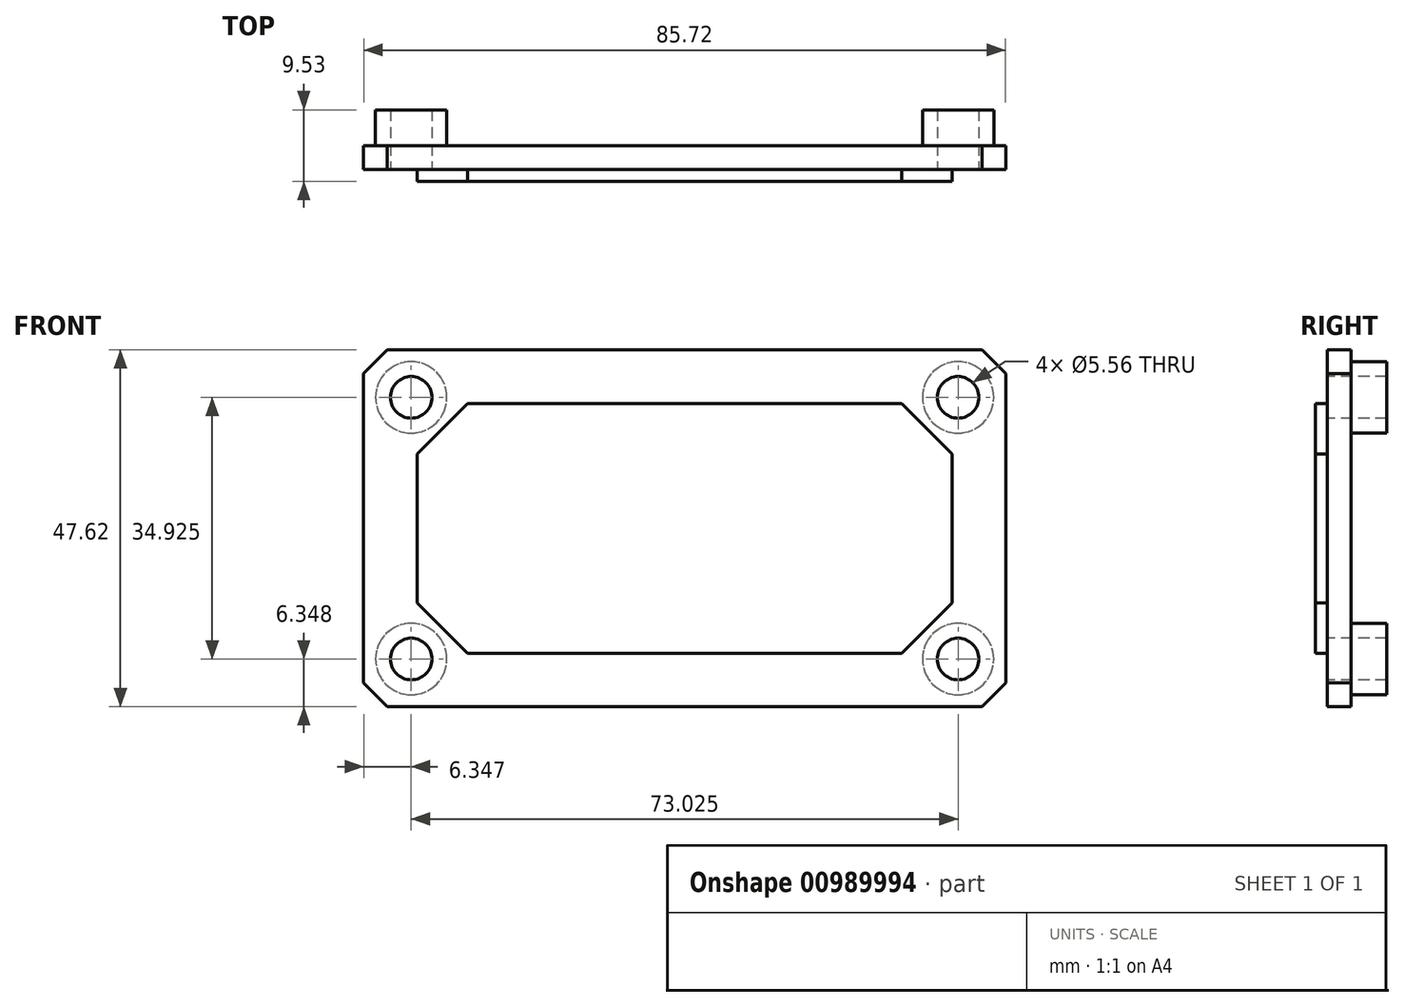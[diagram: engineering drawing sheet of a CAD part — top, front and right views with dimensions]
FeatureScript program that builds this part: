
annotation { "Feature Type Name" : "Feature", "Feature Type Description" : "" }
export const myFeature = defineFeature(function(context is Context, id is Id, definition is map)
    precondition{}
    {
        {
            var Q0;
            Q0=qCreatedBy(makeId("Front.planeOp"),FACE);
            var sketch = newSketch(context, id + "F0", { "sketchPlane" : qUnion([Q0])});
            skLineSegment(sketch, "E0.bottom", {"start": v(-42.86, 23.81) * mm, "end": v(42.86, 23.81) * mm});
            skLineSegment(sketch, "E0.top", {"start": v(-42.86, -23.81) * mm, "end": v(42.86, -23.81) * mm});
            skLineSegment(sketch, "E0.left", {"start": v(-42.86, 23.81) * mm, "end": v(-42.86, -23.81) * mm});
            skLineSegment(sketch, "E0.right", {"start": v(42.86, 23.81) * mm, "end": v(42.86, -23.81) * mm});
            skPoint(sketch, "E0.middle", {"position": v(0, 0) * mm});
            skLineSegment(sketch, "E1", {"start": v(-19.05, 0) * mm, "end": v(19.05, 0) * mm});
            skCircle(sketch, "E2", {"center": v(19.05, 0) * mm, "radius": 17.46 * mm});
            skCircle(sketch, "E3", {"center": v(-19.05, 0) * mm, "radius": 17.46 * mm});
            skCircle(sketch, "E4", {"center": v(-19.05, 0) * mm, "radius": 23.81 * mm, "construction": true});
            skLineSegment(sketch, "E5.0", {"start": v(-36.51, 17.46) * mm, "end": v(36.51, 17.46) * mm});
            skLineSegment(sketch, "E5.1", {"start": v(-36.51, 17.46) * mm, "end": v(-36.51, -17.46) * mm});
            skLineSegment(sketch, "E5.2", {"start": v(-36.51, -17.46) * mm, "end": v(36.51, -17.46) * mm});
            skLineSegment(sketch, "E5.3", {"start": v(36.51, 17.46) * mm, "end": v(36.51, -17.46) * mm});
            skCircle(sketch, "E6", {"center": v(-36.51, 17.46) * mm, "radius": 6.35 * mm, "construction": true});
            skCircle(sketch, "E7", {"center": v(-36.51, 17.46) * mm, "radius": 2.25 * mm});
            skCircle(sketch, "E8", {"center": v(-36.51, 17.46) * mm, "radius": 3.97 * mm});
            skLineSegment(sketch, "E9", {"start": v(-39.69, 23.81) * mm, "end": v(-42.86, 20.64) * mm});
            skCircle(sketch, "E10", {"center": v(-19.05, 0) * mm, "radius": 15.08 * mm});
            skCircle(sketch, "E11", {"center": v(19.05, 0) * mm, "radius": 15.08 * mm});
            skCircle(sketch, "E12", {"center": v(-19.05, 0) * mm, "radius": 11.11 * mm});
            skCircle(sketch, "E13", {"center": v(19.05, 0) * mm, "radius": 11.11 * mm});
            skCircle(sketch, "E14", {"center": v(19.05, 0) * mm, "radius": 23.81 * mm});
            skCircle(sketch, "E15", {"center": v(-36.51, -17.46) * mm, "radius": 2.25 * mm});
            skCircle(sketch, "E16", {"center": v(36.51, 17.46) * mm, "radius": 2.25 * mm});
            skCircle(sketch, "E17", {"center": v(36.51, -17.46) * mm, "radius": 2.25 * mm});
            skLineSegment(sketch, "E18.0", {"start": v(-35.72, 16.67) * mm, "end": v(35.72, 16.67) * mm});
            skLineSegment(sketch, "E18.1", {"start": v(-35.72, 16.67) * mm, "end": v(-35.72, -16.67) * mm});
            skLineSegment(sketch, "E18.2", {"start": v(-35.72, -16.67) * mm, "end": v(35.72, -16.67) * mm});
            skLineSegment(sketch, "E18.3", {"start": v(35.72, 16.67) * mm, "end": v(35.72, -16.67) * mm});
            skLineSegment(sketch, "E19", {"start": v(-29.37, 17.46) * mm, "end": v(-36.51, 10.32) * mm});
            skLineSegment(sketch, "E20", {"start": v(-28.99, 16.67) * mm, "end": v(-35.72, 9.94) * mm});
            skCircle(sketch, "E21", {"center": v(-29.88, 15.78) * mm, "radius": 0.8 * mm});
            skLineSegment(sketch, "E22", {"start": v(28.99, 16.67) * mm, "end": v(35.72, 9.94) * mm});
            skLineSegment(sketch, "E23", {"start": v(35.72, -9.94) * mm, "end": v(28.99, -16.67) * mm});
            skLineSegment(sketch, "E24", {"start": v(-28.99, -16.67) * mm, "end": v(-35.72, -9.94) * mm});
            skCircle(sketch, "E25", {"center": v(-36.51, 17.46) * mm, "radius": 4.76 * mm});
            skCircle(sketch, "E26", {"center": v(-36.51, -17.46) * mm, "radius": 4.76 * mm});
            skCircle(sketch, "E27", {"center": v(36.51, 17.46) * mm, "radius": 4.76 * mm});
            skCircle(sketch, "E28", {"center": v(36.51, -17.46) * mm, "radius": 4.76 * mm});
            skCircle(sketch, "E29", {"center": v(-36.51, 17.46) * mm, "radius": 2.78 * mm});
            skCircle(sketch, "E30", {"center": v(-36.51, -17.46) * mm, "radius": 2.78 * mm});
            skCircle(sketch, "E31", {"center": v(36.51, -17.46) * mm, "radius": 2.78 * mm});
            skCircle(sketch, "E32", {"center": v(36.51, 17.46) * mm, "radius": 2.78 * mm});
            skSolve(sketch);
        }
        {
            var Q0;
            Q0=qCreatedBy(makeId("Right.planeOp"),FACE);
            var Q1;
            Q1=sQuery(id+"F0.wireOp",VERTEX,"E1.start");
            cPlane(context, id + "F1", {"entities" : qUnion([Q0, Q1]), "cplaneType" : CPlaneType.PLANE_POINT, "offset" : 25.4 * mm, "width" : 152.4 * mm, "height" : 152.4 * mm});
        }
        {
            var Q0;
            Q0=qCreatedBy(id+"F1.planeOp",FACE);
            var sketch = newSketch(context, id + "F2", { "sketchPlane" : qUnion([Q0])});
            skLineSegment(sketch, "E33", {"start": v(-30.16, 0) * mm, "end": v(12.8, 0) * mm, "construction": true});
            skLineSegment(sketch, "E34", {"start": v(-30.16, 17.46) * mm, "end": v(-30.16, -17.46) * mm});
            skLineSegment(sketch, "E35", {"start": v(-30.16, 15.08) * mm, "end": v(-30.16, -15.08) * mm});
            skLineSegment(sketch, "E36", {"start": v(-30.16, 15.08) * mm, "end": v(0, 14.55) * mm});
            skLineSegment(sketch, "E37", {"start": v(0, 14.55) * mm, "end": v(0, -14.55) * mm});
            skLineSegment(sketch, "E38", {"start": v(0, -14.55) * mm, "end": v(-30.16, -15.08) * mm});
            skLineSegment(sketch, "E39", {"start": v(-30.16, 17.46) * mm, "end": v(0, 17.46) * mm});
            skLineSegment(sketch, "E40", {"start": v(0, 17.46) * mm, "end": v(0, 23.81) * mm});
            skLineSegment(sketch, "E41", {"start": v(0, 23.81) * mm, "end": v(3.17, 23.81) * mm});
            skLineSegment(sketch, "E42", {"start": v(3.17, 23.81) * mm, "end": v(3.18, -23.81) * mm});
            skLineSegment(sketch, "E43", {"start": v(-30.16, -17.46) * mm, "end": v(0, -17.46) * mm});
            skLineSegment(sketch, "E44", {"start": v(0, -17.46) * mm, "end": v(0, -23.81) * mm});
            skLineSegment(sketch, "E45", {"start": v(0, -23.81) * mm, "end": v(3.18, -23.81) * mm});
            skLineSegment(sketch, "E46", {"start": v(3.17, 17.46) * mm, "end": v(33.34, 17.46) * mm});
            skLineSegment(sketch, "E47", {"start": v(33.34, 17.46) * mm, "end": v(33.34, 15.08) * mm});
            skLineSegment(sketch, "E48", {"start": v(33.34, 15.08) * mm, "end": v(3.17, 14.55) * mm});
            skSolve(sketch);
        }
        {
            var Q0;
            Q0=qCreatedBy(makeId("Front.planeOp"),FACE);
            var sketch = newSketch(context, id + "F3", { "sketchPlane" : qUnion([Q0])});
            skLineSegment(sketch, "E49.0", {"start": v(-42.86, 23.81) * mm, "end": v(42.86, 23.81) * mm});
            skLineSegment(sketch, "E49.1", {"start": v(42.86, 23.81) * mm, "end": v(42.86, -23.81) * mm});
            skLineSegment(sketch, "E49.2", {"start": v(-42.86, -23.81) * mm, "end": v(42.86, -23.81) * mm});
            skLineSegment(sketch, "E49.3", {"start": v(-42.86, 23.81) * mm, "end": v(-42.86, -23.81) * mm});
            skSolve(sketch);
        }
        {
            var Q0;
            Q0=qSketchRegion(id+"F3",true);
            var Q1;
            Q1=sQuery(id+"F2.wireOp",VERTEX,"E41.end");
            extrude(context, id + "F4", {"entities" : qUnion([Q0]), "endBound" : BoundingType.UP_TO_VERTEX, "oppositeDirection" : true, "depth" : 25.4 * mm, "endBoundEntityVertex" : qUnion([Q1]), "offsetDistance" : 25.4 * mm});
        }
        {
            var Q0;
            Q0=qCreatedBy(makeId("Front.planeOp"),FACE);
            var sketch = newSketch(context, id + "F5", { "sketchPlane" : qUnion([Q0])});
            skLineSegment(sketch, "E50.0", {"start": v(-28.99, 16.67) * mm, "end": v(-35.72, 9.94) * mm});
            skLineSegment(sketch, "E50.1", {"start": v(-28.99, 16.67) * mm, "end": v(28.99, 16.67) * mm});
            skLineSegment(sketch, "E50.2", {"start": v(28.99, 16.67) * mm, "end": v(35.72, 9.94) * mm});
            skLineSegment(sketch, "E50.3", {"start": v(35.72, 9.94) * mm, "end": v(35.72, -9.94) * mm});
            skLineSegment(sketch, "E50.4", {"start": v(35.72, -9.94) * mm, "end": v(28.99, -16.67) * mm});
            skLineSegment(sketch, "E50.5", {"start": v(-28.99, -16.67) * mm, "end": v(28.99, -16.67) * mm});
            skLineSegment(sketch, "E50.6", {"start": v(-28.99, -16.67) * mm, "end": v(-35.72, -9.94) * mm});
            skLineSegment(sketch, "E50.7", {"start": v(-35.72, 9.94) * mm, "end": v(-35.72, -9.94) * mm});
            skPoint(sketch, "E51.orphan", {"position": v(-35.72, 16.67) * mm});
            skPoint(sketch, "E52.orphan", {"position": v(-35.72, -16.67) * mm});
            skPoint(sketch, "E53.orphan", {"position": v(35.72, -16.67) * mm});
            skPoint(sketch, "E54.orphan", {"position": v(35.72, 16.67) * mm});
            skSolve(sketch);
        }
        {
            var Q0;
            Q0=qSketchRegion(id+"F5",true);
            extrude(context, id + "F6", {"entities" : qUnion([Q0]), "operationType" : NewBodyOperationType.ADD, "depth" : 1.59 * mm, "offsetDistance" : 25.4 * mm});
        }
        {
            var Q0;
            Q0=qCreatedBy(makeId("Front.planeOp"),FACE);
            var sketch = newSketch(context, id + "F7", { "sketchPlane" : qUnion([Q0])});
            skCircle(sketch, "E55.0", {"center": v(36.51, 17.46) * mm, "radius": 4.76 * mm});
            skCircle(sketch, "E55.1", {"center": v(-36.51, 17.46) * mm, "radius": 4.76 * mm});
            skCircle(sketch, "E55.2", {"center": v(-36.51, -17.46) * mm, "radius": 4.76 * mm});
            skCircle(sketch, "E55.3", {"center": v(36.51, -17.46) * mm, "radius": 4.76 * mm});
            skSolve(sketch);
        }
        {
            var Q0;
            Q0=qSketchRegion(id+"F7",true);
            extrude(context, id + "F8", {"entities" : qUnion([Q0]), "operationType" : NewBodyOperationType.ADD, "oppositeDirection" : true, "depth" : 7.94 * mm, "offsetDistance" : 25.4 * mm});
        }
        {
            var Q0;
            Q0=qCreatedBy(makeId("Front.planeOp"),FACE);
            var sketch = newSketch(context, id + "F9", { "sketchPlane" : qUnion([Q0])});
            skCircle(sketch, "E56.0", {"center": v(36.51, 17.46) * mm, "radius": 2.78 * mm});
            skCircle(sketch, "E56.1", {"center": v(36.51, -17.46) * mm, "radius": 2.78 * mm});
            skCircle(sketch, "E56.2", {"center": v(-36.51, 17.46) * mm, "radius": 2.78 * mm});
            skCircle(sketch, "E56.3", {"center": v(-36.51, -17.46) * mm, "radius": 2.78 * mm});
            skSolve(sketch);
        }
        {
            var Q0;
            Q0=qSketchRegion(id+"F9",true);
            extrude(context, id + "F10", {"entities" : qUnion([Q0]), "operationType" : NewBodyOperationType.REMOVE, "endBound" : BoundingType.UP_TO_NEXT, "oppositeDirection" : true, "depth" : 25.4 * mm, "offsetDistance" : 25.4 * mm});
        }
        {
            var Q0;
            Q0=makeQuery(id+"F4.opExtrude","SWEPT_EDGE",EDGE,{"disambiguationData":[OSD([sQuery(id+"F3.wireOp",EDGE,"E49.1"),sQuery(id+"F3.wireOp",EDGE,"E49.2")])]});
            var Q1;
            Q1=makeQuery(id+"F4.opExtrude","SWEPT_EDGE",EDGE,{"disambiguationData":[OSD([sQuery(id+"F3.wireOp",EDGE,"E49.0"),sQuery(id+"F3.wireOp",EDGE,"E49.1")])]});
            var Q2;
            Q2=makeQuery(id+"F4.opExtrude","SWEPT_EDGE",EDGE,{"disambiguationData":[OSD([sQuery(id+"F3.wireOp",EDGE,"E49.2"),sQuery(id+"F3.wireOp",EDGE,"E49.3")])]});
            var Q3;
            Q3=makeQuery(id+"F4.opExtrude","SWEPT_EDGE",EDGE,{"disambiguationData":[OSD([sQuery(id+"F3.wireOp",EDGE,"E49.0"),sQuery(id+"F3.wireOp",EDGE,"E49.3")])]});
            chamfer(context, id + "F11", {"entities" : qUnion([Q0, Q1, Q2, Q3]), "width" : 3.17 * mm, "tangentPropagation" : true});
        }
    });
